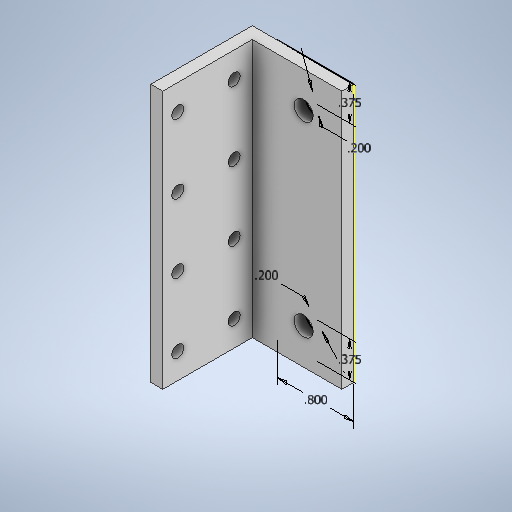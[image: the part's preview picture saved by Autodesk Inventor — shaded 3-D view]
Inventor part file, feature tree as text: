
AUTODESK INVENTOR PART (.ipt)
format: ipt  version: 2025.1 (Build 291241000, 241)  size: 307,200 bytes
history: native  units: in
note: dims shown in document units (in); Inventor stores cm internally (conversion verified against a paired STEP export)
features: extrude x6, sketch x6, direct_edit x3, move_body x3
ambient origin geometry x8: Origin, YZ Plane, XZ Plane, XY Plane, X Axis, Y Axis, Z Axis, Center Point
bodies: Solid1 (feature_tree)
feature tree (18):
  extrude  "Extrusion1"  Depth=1.0625in
  extrude  "Extrusion4"  Depth=0.125in
  direct_edit  "Direct Edit1"
  extrude  "Extrusion5"  Depth=0.535in
  direct_edit  "Direct Edit2"
  extrude  "Extrusion6"  Depth=0.125in
  direct_edit  "Direct Edit3"
  extrude  "Extrusion7"  Depth=0.125in
  extrude  "Extrusion8"  Depth=0.125in TaperAngle=0.0deg
  sketch  "Sketch1"  dims[d0=1.0625in d1=1.0625in]
  sketch  "Sketch4"  dims[d2=0.125in d4=0.125in]
  sketch  "Sketch5"  dims[d5=0.723in d6=0.0in d23=0.535in]
  sketch  "Sketch6"  dims[d24=0.315in d25=0.125in]
  sketch  "Sketch7"  dims[d26=0.59in d27=0.125in]
  sketch  "Sketch8"  dims[d28=0.723in d29=0.0in d30=0.0in d31=0.0in d32=0.535in d33=0.535in d34=0.315in d35=0.125in d36=0.59in d37=0.125in d38=0.723in d39=0.0in d40=0.0in d41=0.0in d42=0.7225in d43=0.535in d44=0.315in d45=0.125in d46=0.59in d47=0.125in d48=0.723in d49=0.0in d50=0.0in d51=0.0in d52=0.7225in d53=0.535in d54=0.315in d55=0.125in d56=0.59in d57=0.125in d58=0.723in d59=0.0in d60=0.8in d61=0.375in d62=0.375in d63=0.2in d64=0.2in d65=0.723in d66=0.0in]
  move_body  "Move1"
  move_body  "Move2"
  move_body  "Move3"
